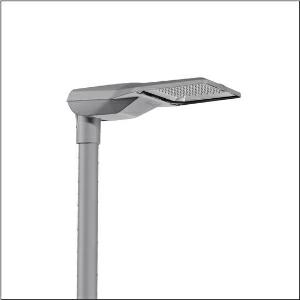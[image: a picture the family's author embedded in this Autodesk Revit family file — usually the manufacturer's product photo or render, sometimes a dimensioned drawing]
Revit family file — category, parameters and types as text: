
# Revit family: streetlight_sl_21_iq_midi___stw1_0a_5xe3e21g08nb_ca38
name_source: partatom
category: Lighting Fixtures
units: mm (PartAtom-declared; Revit-internal decimal feet)

## family parameters
Cut with Voids When Loaded = No
Host = Face
Light Source = No
Part Type = Normal
Room Calculation Point = No
Round Connector Dimension = Use Diameter
Shared = No

## types (1)
- --- (1 x LED, 19210 lm, 155.5 W, 2200K)
    Apparent Load = 155 VA
    CIE Flux Codes = 39 75 98 100 100
    Color Rendering = 70
    Color Temperature = 2200K
    Default Elevation = 1800 mm
    Description = Streetlight SL 21 iQ midi, mast luminaire, primary light control with lens, of PMMA, primary optical cover: cover, of toughened safety glass, transparent, light distribution: STW1.0a, light emission: direct distribution, primary light characteristic: asymmetric, installation type: post-top, side-entry, LED, High Power LED, rated luminous flux: 19.210lm, luminous efficacy: 124lm/W, light colour: 722, colour temperature: 2200K, control: Street-Remote, Auto-Match, Temp-Guard, Lumen-Switch, Night-Set, Smart-Wire, Light-Fading, Desk-Remote (wireless, voltage-free reading and setting of iQ features in the workshop via application-optimized NFC function/RFID function), optimised constant luminous flux control (CLO 2.0), presetting dimming linear, mains connection: 230..240V, AC, 50/60Hz, start of lifetime: 156W, end of service life: 162W, reduction: 69W, luminaire housing, of diecast aluminium, powder-coated, Siteco® metallic grey (DB 702S), corrosivity category C5 mid according to DIN EN ISO 12944, please order mast flange separately, inclination adjustable: 0°, 5°, 10°, 15°, sealing non-destructively replaceable, multi-level sealing system, length: 644mm, width: 335mm, height: 110mm, mast flange for spigot size: 42mm (side-entry): 5XC10008XM4, 60/48mm (side-entry/post-top): 5XC10108XM2, 76/60mm (side-entry/post-top): 5XC10108XM1, protection rating (complete): IP66, insulation class (complete): insulation class II (safety insulation), certification: CE, ENEC, ENEC+, VDE, impact resistance: IK09, permissible operating ambient temperature for outdoor applications: -40..+50°C, standard-compliant lighting for roads and squares, packaging unit: 1 piece

Light Distribution: STW1.0a
    Height = 111 mm
    Lamp = 1 x LED
    Lamp Light Flux = 19210 lm
    Lamp Power = 155.5 W
    Lamp count = 1
    Length = 644 mm
    Luminous efficacy = 124 lm/W
    Manufacturer = Siteco
    ModVariant = No
    Model = 5XE3E21G08NB
    Number of Poles = 1
    OnlyDefault = Yes
    Power Factor = 1
    Product Name = Streetlight SL 21 iQ midi | STW1.0a
    Product group = mast luminaire | pylon top
    ProductGroupID = 6100
    Protection Class = Protection class II
    Protection Degree = IP 66
    RLX_Detail_Level = 1
    RLX_Emergency_Light_Flux = 0 lm
    RLX_Emergency_Type = 0
    RLX_Emergency_Type_DB = No
    RlxData = <blob elided: 91301 chars, md5=70d929d9>
    Socket = socket
    Standby Power = 0 W
    System Light Flux = 19210 lm
    System Power = 155 W
    Type Comments = factory setting: luminous flux: 100 % | dim-lin: 254 | 823 mA
    Type Image = l_1004298.jpg
    URL = http://relux.com
    VarID = @adj_102545
    Voltage = 0 V
    Weight = 0.00 kg
    Width = 336 mm

## geometry (parser evidence)
native form markers: Blend x4, Sweep x10
no freeform markers — native parametric forms only
